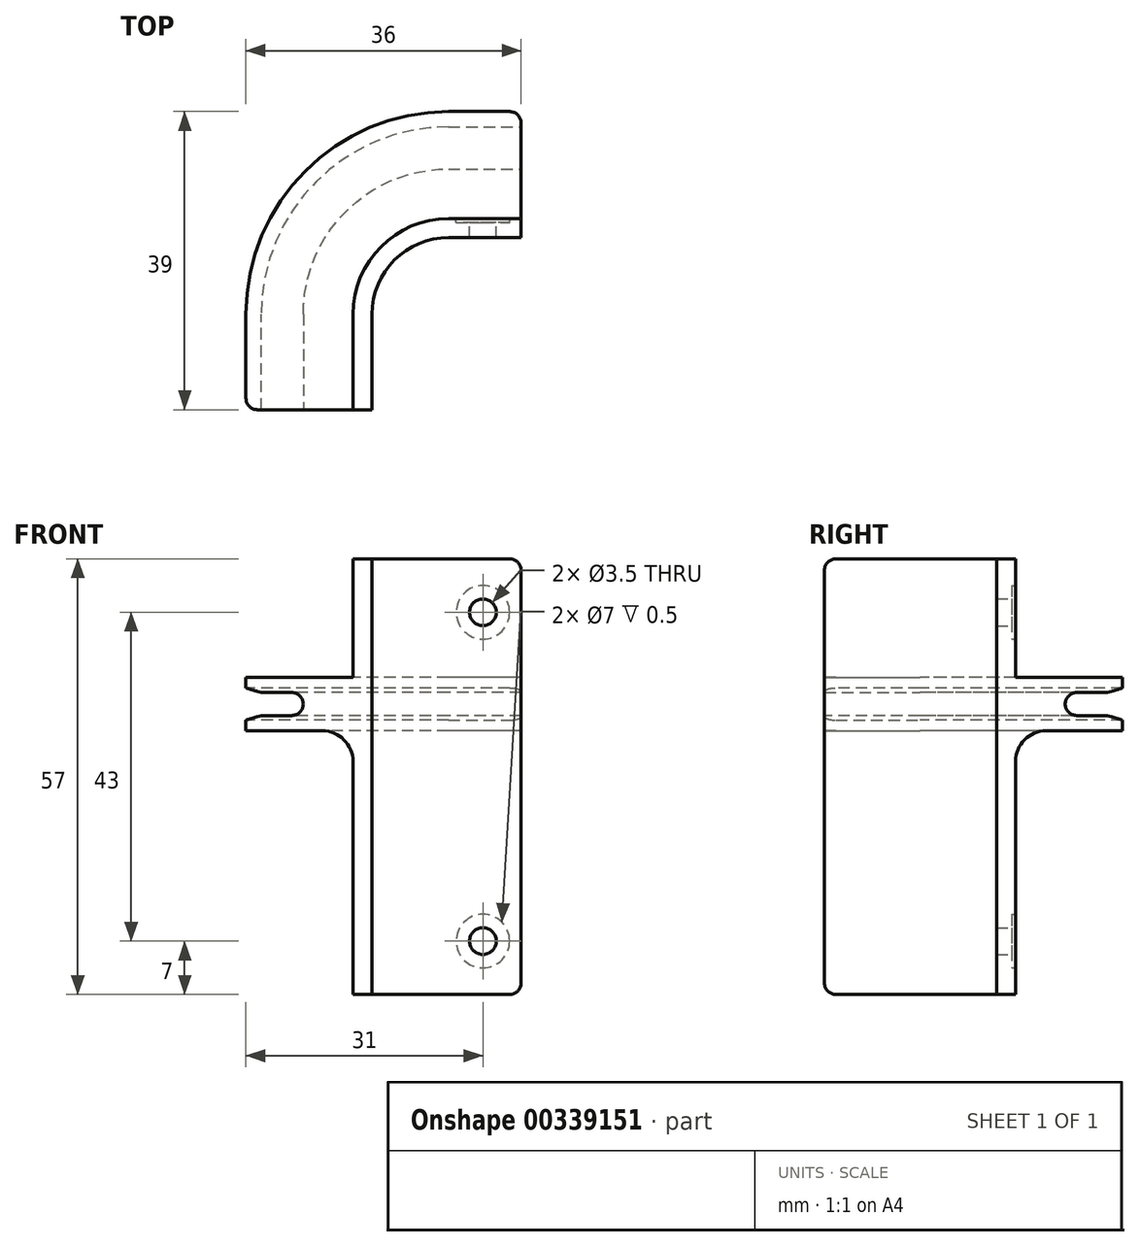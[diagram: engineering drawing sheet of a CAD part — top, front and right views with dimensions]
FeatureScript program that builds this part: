
annotation { "Feature Type Name" : "Feature", "Feature Type Description" : "" }
export const myFeature = defineFeature(function(context is Context, id is Id, definition is map)
    precondition{}
    {
        {
            var Q0;
            Q0=qCreatedBy(makeId("Top.planeOp"),FACE);
            var sketch = newSketch(context, id + "F0", { "sketchPlane" : qUnion([Q0])});
            skArc(sketch, "E0", {"start": v(0, 10) * mm, "mid": v(-7.07, 7.07) * mm, "end": v(-10, 0) * mm});
            skLineSegment(sketch, "E1", {"start": v(0, 10) * mm, "end": v(9.5, 10) * mm});
            skArc(sketch, "E2", {"start": v(0, 12.5) * mm, "mid": v(-8.84, 8.84) * mm, "end": v(-12.5, 0) * mm});
            skLineSegment(sketch, "E3", {"start": v(-12.5, 0) * mm, "end": v(-12.5, -12.5) * mm});
            skLineSegment(sketch, "E4", {"start": v(0, 12.5) * mm, "end": v(9.5, 12.5) * mm});
            skLineSegment(sketch, "E5", {"start": v(-10, 0) * mm, "end": v(-10, -12.5) * mm});
            skLineSegment(sketch, "E6", {"start": v(-10, -12.5) * mm, "end": v(-12.5, -12.5) * mm});
            skLineSegment(sketch, "E7", {"start": v(9.5, 12.5) * mm, "end": v(9.5, 10) * mm});
            skSolve(sketch);
        }
        {
            var Q0;
            Q0=makeQuery(id+"F0.imprint","IMPRINT",FACE,{"disambiguationData":[TD([[makeQuery(id+"F0.imprint","IMPRINT",EDGE,{"derivedFrom":sQuery(id+"F0.wireOp",EDGE,"E0")}),-1.0]])]});
            extrude(context, id + "F1", {"entities" : qUnion([Q0]), "depth" : 40 * mm});
        }
        {
            var Q0;
            Q0=makeQuery(id+"F1.opExtrude","SWEPT_FACE",FACE,{"disambiguationData":[OSD([sQuery(id+"F0.wireOp",EDGE,"E4")])]});
            var sketch = newSketch(context, id + "F2", { "sketchPlane" : qUnion([Q0])});
            skLineSegment(sketch, "E8", {"start": v(-9.5, 24.5) * mm, "end": v(-5.72, 24.5) * mm});
            skLineSegment(sketch, "E9", {"start": v(-9.5, 17.5) * mm, "end": v(-5.74, 17.5) * mm});
            skLineSegment(sketch, "E10", {"start": v(-9.5, 22.5) * mm, "end": v(-5.74, 22.5) * mm});
            skLineSegment(sketch, "E11", {"start": v(-9.5, 19.5) * mm, "end": v(-5.73, 19.5) * mm});
            skPoint(sketch, "E12.orphan", {"position": v(0, 22.5) * mm});
            skPoint(sketch, "E13.orphan", {"position": v(0, 19.5) * mm});
            skPoint(sketch, "E14.orphan", {"position": v(0, 23) * mm});
            skPoint(sketch, "E15.end.orphan", {"position": v(0, 25) * mm});
            skPoint(sketch, "E16.start.orphan", {"position": v(0, 20) * mm});
            skLineSegment(sketch, "E17", {"start": v(-5.72, 24.5) * mm, "end": v(0, 24.5) * mm});
            skLineSegment(sketch, "E18", {"start": v(-5.74, 22.5) * mm, "end": v(0, 22.5) * mm});
            skLineSegment(sketch, "E19", {"start": v(-5.73, 19.5) * mm, "end": v(0, 19.5) * mm});
            skLineSegment(sketch, "E20", {"start": v(-5.74, 17.5) * mm, "end": v(0, 17.5) * mm});
            skSolve(sketch);
        }
        {
            var Q0;
            {var subQ0=sQuery(id+"F2.wireOp",EDGE,"E10");Q0=makeQuery(id+"F2.imprint","IMPRINT",FACE,{"disambiguationData":[TD([[makeQuery(id+"F2.imprint","IMPRINT",EDGE,{"derivedFrom":subQ0}),-1.0]])]});}
            extrude(context, id + "F3", {"entities" : qUnion([Q0]), "operationType" : NewBodyOperationType.ADD, "depth" : 6.5 * mm});
        }
        {
            var Q0;
            {var subQ0=sQuery(id+"F2.wireOp",EDGE,"E8");Q0=makeQuery(id+"F2.imprint","IMPRINT",FACE,{"disambiguationData":[TD([[makeQuery(id+"F2.imprint","IMPRINT",EDGE,{"derivedFrom":subQ0}),-1.0]])]});}
            var Q1;
            {var subQ0=sQuery(id+"F2.wireOp",EDGE,"E9");Q1=makeQuery(id+"F2.imprint","IMPRINT",FACE,{"disambiguationData":[TD([[makeQuery(id+"F2.imprint","IMPRINT",EDGE,{"derivedFrom":subQ0}),1.0]])]});}
            extrude(context, id + "F4", {"entities" : qUnion([Q0, Q1]), "operationType" : NewBodyOperationType.ADD, "depth" : 14 * mm});
        }
        {
            var Q0;
            {var subQ4=sQuery(id+"F2.wireOp",EDGE,"E8");Q0=makeQuery(id+"F2.imprint","IMPRINT",FACE,{"disambiguationData":[TD([[makeQuery(id+"F2.imprint","IMPRINT",EDGE,{"derivedFrom":subQ4}),1.0]])]});}
            var sketch = newSketch(context, id + "F5", { "sketchPlane" : qUnion([Q0])});
            skCircle(sketch, "E21", {"center": v(-4.5, 33) * mm, "radius": 3.5 * mm});
            skCircle(sketch, "E22", {"center": v(-4.5, 33) * mm, "radius": 1.75 * mm});
            skSolve(sketch);
        }
        {
            var Q0;
            Q0=makeQuery(id+"F5.imprint","IMPRINT",FACE,{"disambiguationData":[TD([[makeQuery(id+"F5.imprint","IMPRINT",EDGE,{"derivedFrom":sQuery(id+"F5.wireOp",EDGE,"E21")}),1.0]])]});
            extrude(context, id + "F6", {"entities" : qUnion([Q0]), "operationType" : NewBodyOperationType.REMOVE, "oppositeDirection" : true, "depth" : 0.5 * mm});
        }
        {
            var Q0;
            Q0=makeQuery(id+"F5.imprint","IMPRINT",FACE,{"disambiguationData":[TD([[makeQuery(id+"F5.imprint","IMPRINT",EDGE,{"derivedFrom":sQuery(id+"F5.wireOp",EDGE,"E22")}),1.0]])]});
            extrude(context, id + "F7", {"entities" : qUnion([Q0]), "operationType" : NewBodyOperationType.REMOVE, "oppositeDirection" : true, "depth" : 25 * mm});
        }
        {
            var Q0;
            Q0=makeQuery(id+"F1.opExtrude","CAP_FACE",FACE,{"disambiguationData":[OSD([sQuery(id+"F0.wireOp",EDGE,"E0"),sQuery(id+"F0.wireOp",EDGE,"E1"),sQuery(id+"F0.wireOp",EDGE,"E2"),sQuery(id+"F0.wireOp",EDGE,"E3"),sQuery(id+"F0.wireOp",EDGE,"E4"),sQuery(id+"F0.wireOp",EDGE,"E5"),sQuery(id+"F0.wireOp",EDGE,"E6"),sQuery(id+"F0.wireOp",EDGE,"E7")])],"isStart":true});
            extrude(context, id + "F8", {"entities" : qUnion([Q0]), "operationType" : NewBodyOperationType.ADD, "depth" : 17 * mm});
        }
        {
            var Q0;
            {var subQ0=sQuery(id+"F0.wireOp",EDGE,"E4");Q0=makeQuery(id+"F8.boolean.opBoolean","MERGE",FACE,{"derivedFrom":[makeQuery(id+"F3.boolean.opBoolean","SPLIT",FACE,{"disambiguationData":[TD([makeQuery(id+"F3.opExtrude","SWEPT_FACE",FACE,{"disambiguationData":[OSD([sQuery(id+"F2.wireOp",EDGE,"E11"),sQuery(id+"F2.wireOp",EDGE,"E19")])]})])],"derivedFrom":makeQuery(id+"F1.opExtrude","SWEPT_FACE",FACE,{"disambiguationData":[OSD([subQ0])]})}),makeQuery(id+"F8.opExtrude","SWEPT_FACE",FACE,{"disambiguationData":[OSD([subQ0])]})]});}
            var sketch = newSketch(context, id + "F9", { "sketchPlane" : qUnion([Q0])});
            skCircle(sketch, "E23", {"center": v(-4.5, -10) * mm, "radius": 3.5 * mm});
            skCircle(sketch, "E24", {"center": v(-4.5, -10) * mm, "radius": 1.75 * mm});
            skSolve(sketch);
        }
        {
            var Q0;
            Q0=makeQuery(id+"F9.imprint","IMPRINT",FACE,{"disambiguationData":[TD([[makeQuery(id+"F9.imprint","IMPRINT",EDGE,{"derivedFrom":sQuery(id+"F9.wireOp",EDGE,"E24")}),1.0]])]});
            extrude(context, id + "F10", {"entities" : qUnion([Q0]), "operationType" : NewBodyOperationType.REMOVE, "oppositeDirection" : true, "depth" : 3 * mm});
        }
        {
            var Q0;
            Q0=makeQuery(id+"F9.imprint","IMPRINT",FACE,{"disambiguationData":[TD([[makeQuery(id+"F9.imprint","IMPRINT",EDGE,{"derivedFrom":sQuery(id+"F9.wireOp",EDGE,"E23")}),1.0]])]});
            extrude(context, id + "F11", {"entities" : qUnion([Q0]), "operationType" : NewBodyOperationType.REMOVE, "oppositeDirection" : true, "depth" : 0.5 * mm});
        }
        {
            var Q0;
            {var subQ0=sQuery(id+"F0.wireOp",EDGE,"E3");Q0=makeQuery(id+"F8.boolean.opBoolean","MERGE",FACE,{"derivedFrom":[makeQuery(id+"F1.opExtrude","SWEPT_FACE",FACE,{"disambiguationData":[OSD([subQ0])]}),makeQuery(id+"F8.opExtrude","SWEPT_FACE",FACE,{"disambiguationData":[OSD([subQ0])]})]});}
            var sketch = newSketch(context, id + "F12", { "sketchPlane" : qUnion([Q0])});
            skLineSegment(sketch, "E25", {"start": v(12.5, 24.5) * mm, "end": v(0, 24.5) * mm});
            skLineSegment(sketch, "E26", {"start": v(12.5, 22.5) * mm, "end": v(0, 22.5) * mm});
            skLineSegment(sketch, "E27", {"start": v(12.5, 19.5) * mm, "end": v(0, 19.5) * mm});
            skLineSegment(sketch, "E28", {"start": v(12.5, 17.5) * mm, "end": v(0, 17.5) * mm});
            skSolve(sketch);
        }
        {
            var Q0;
            {var subQ0=sQuery(id+"F12.wireOp",EDGE,"E26");Q0=makeQuery(id+"F12.imprint","IMPRINT",FACE,{"disambiguationData":[TD([[makeQuery(id+"F12.imprint","IMPRINT",EDGE,{"derivedFrom":subQ0}),1.0]])]});}
            extrude(context, id + "F13", {"entities" : qUnion([Q0]), "operationType" : NewBodyOperationType.ADD, "depth" : 6.5 * mm});
        }
        {
            var Q0;
            {var subQ0=sQuery(id+"F12.wireOp",EDGE,"E25");Q0=makeQuery(id+"F12.imprint","IMPRINT",FACE,{"disambiguationData":[TD([[makeQuery(id+"F12.imprint","IMPRINT",EDGE,{"derivedFrom":subQ0}),1.0]])]});}
            var Q1;
            {var subQ0=sQuery(id+"F12.wireOp",EDGE,"E27");Q1=makeQuery(id+"F12.imprint","IMPRINT",FACE,{"disambiguationData":[TD([[makeQuery(id+"F12.imprint","IMPRINT",EDGE,{"derivedFrom":subQ0}),1.0]])]});}
            extrude(context, id + "F14", {"entities" : qUnion([Q0, Q1]), "operationType" : NewBodyOperationType.ADD, "depth" : 14 * mm});
        }
        {
            var Q0;
            {var subQ0=sQuery(id+"F0.wireOp",EDGE,"E3");var subQ1=sQuery(id+"F0.wireOp",EDGE,"E2");var subQ2=makeQuery(id+"F8.boolean.opBoolean","MERGE",EDGE,{"derivedFrom":[makeQuery(id+"F1.opExtrude","SWEPT_EDGE",EDGE,{"disambiguationData":[OSD([subQ1,subQ0])]}),makeQuery(id+"F8.opExtrude","SWEPT_EDGE",EDGE,{"disambiguationData":[OSD([subQ1,subQ0])]})]});Q0=makeQuery(id+"F14.boolean.opBoolean","MERGE",FACE,{"derivedFrom":[makeQuery(id+"F13.opExtrude","SWEPT_FACE",FACE,{"disambiguationData":[OSD([subQ1,subQ0])]}),makeQuery(id+"F14.opExtrude","SWEPT_FACE",FACE,{"disambiguationData":[OSD([subQ1,subQ0]),TDD([makeQuery(id+"F12.imprint","IMPRINT",EDGE,{"disambiguationData":[TD([[makeQuery(id+"F12.imprint","INTERSECT",VERTEX,{"derivedFrom":[subQ2,sQuery(id+"F12.wireOp",EDGE,"E25")]}),-1.0]])],"derivedFrom":subQ2})])]}),makeQuery(id+"F14.opExtrude","SWEPT_FACE",FACE,{"disambiguationData":[OSD([subQ1,subQ0]),TDD([makeQuery(id+"F12.imprint","IMPRINT",EDGE,{"disambiguationData":[TD([[makeQuery(id+"F12.imprint","INTERSECT",VERTEX,{"derivedFrom":[subQ2,sQuery(id+"F12.wireOp",EDGE,"E27")]}),-1.0]])],"derivedFrom":subQ2})])]})]});}
            var Q1;
            {var subQ0=sQuery(id+"F0.wireOp",EDGE,"E2");Q1=makeQuery(id+"F8.boolean.opBoolean","MERGE",FACE,{"derivedFrom":[makeQuery(id+"F1.opExtrude","SWEPT_FACE",FACE,{"disambiguationData":[OSD([subQ0])]}),makeQuery(id+"F8.opExtrude","SWEPT_FACE",FACE,{"disambiguationData":[OSD([subQ0])]})]});}
            revolve(context, id + "F15", {"operationType" : NewBodyOperationType.ADD, "entities" : qUnion([Q0]), "axis" : qUnion([Q1]), "revolveType" : RevolveType.ONE_DIRECTION, "angle" : 90 * degree});
        }
        {
            var Q0;
            {var subQ0=sQuery(id+"F12.wireOp",EDGE,"E28");var subQ1=sQuery(id+"F0.wireOp",EDGE,"E3");var subQ2=sQuery(id+"F0.wireOp",EDGE,"E2");Q0=makeQuery(id+"F15.opRevolve","SWEPT_EDGE",EDGE,{"disambiguationData":[OSD([subQ2,subQ1,subQ0]),TDD([makeQuery(id+"F14.opExtrude","CAP_VERTEX",VERTEX,{"disambiguationData":[OSD([subQ2,subQ1,subQ0])],"isStart":true})])]});}
            var Q1;
            {var subQ0=sQuery(id+"F12.wireOp",EDGE,"E25");var subQ1=sQuery(id+"F0.wireOp",EDGE,"E3");var subQ2=sQuery(id+"F0.wireOp",EDGE,"E2");Q1=makeQuery(id+"F15.opRevolve","SWEPT_EDGE",EDGE,{"disambiguationData":[OSD([subQ2,subQ1,subQ0]),TDD([makeQuery(id+"F14.opExtrude","CAP_VERTEX",VERTEX,{"disambiguationData":[OSD([subQ2,subQ1,subQ0])],"isStart":true})])]});}
            fillet(context, id + "F16", {"entities" : qUnion([Q0, Q1]), "radius" : 4 * mm, "tangentPropagation" : true, "allowEdgeOverflow" : false});
        }
        {
            var Q0;
            Q0=makeQuery(id+"F14.opExtrude","CAP_EDGE",EDGE,{"disambiguationData":[OSD([sQuery(id+"F12.wireOp",EDGE,"E27")])],"isStart":false});
            chamfer(context, id + "F17", {"entities" : qUnion([Q0]), "chamferType" : ChamferType.TWO_OFFSETS, "width1" : 0.6 * mm, "oppositeDirection" : false, "width2" : 2 * mm, "tangentPropagation" : true});
        }
        {
            var Q0;
            Q0=makeQuery(id+"F14.opExtrude","CAP_EDGE",EDGE,{"disambiguationData":[OSD([sQuery(id+"F12.wireOp",EDGE,"E26")])],"isStart":false});
            chamfer(context, id + "F18", {"entities" : qUnion([Q0]), "chamferType" : ChamferType.TWO_OFFSETS, "width1" : 2 * mm, "oppositeDirection" : false, "width2" : 0.6 * mm, "tangentPropagation" : true});
        }
        {
            var Q0;
            {var subQ0=sQuery(id+"F12.wireOp",EDGE,"E27");var subQ1=sQuery(id+"F0.wireOp",EDGE,"E3");var subQ2=sQuery(id+"F0.wireOp",EDGE,"E2");Q0=makeQuery(id+"F15.opRevolve","SWEPT_EDGE",EDGE,{"disambiguationData":[OSD([subQ2,subQ1,subQ0]),TDD([makeQuery(id+"F13.opExtrude","CAP_VERTEX",VERTEX,{"disambiguationData":[OSD([subQ2,subQ1,subQ0])],"isStart":false})])]});}
            var Q1;
            {var subQ0=sQuery(id+"F12.wireOp",EDGE,"E26");var subQ1=sQuery(id+"F0.wireOp",EDGE,"E3");var subQ2=sQuery(id+"F0.wireOp",EDGE,"E2");Q1=makeQuery(id+"F15.opRevolve","SWEPT_EDGE",EDGE,{"disambiguationData":[OSD([subQ2,subQ1,subQ0]),TDD([makeQuery(id+"F13.opExtrude","CAP_VERTEX",VERTEX,{"disambiguationData":[OSD([subQ2,subQ1,subQ0])],"isStart":false})])]});}
            var Q2;
            {var subQ0=sQuery(id+"F0.wireOp",EDGE,"E7");var subQ1=sQuery(id+"F0.wireOp",EDGE,"E4");var subQ2=makeQuery(id+"F1.opExtrude","SWEPT_EDGE",EDGE,{"disambiguationData":[OSD([subQ1,subQ0])]});Q2=makeQuery(id+"F4.opExtrude","CAP_EDGE",EDGE,{"disambiguationData":[OSD([subQ1,subQ0]),TDD([makeQuery(id+"F2.imprint","IMPRINT",EDGE,{"disambiguationData":[TD([[makeQuery(id+"F2.imprint","INTERSECT",VERTEX,{"derivedFrom":[subQ2,sQuery(id+"F2.wireOp",EDGE,"E8")]}),-1.0]])],"derivedFrom":subQ2})])],"isStart":false});}
            var Q3;
            {var subQ0=sQuery(id+"F0.wireOp",EDGE,"E7");var subQ1=sQuery(id+"F0.wireOp",EDGE,"E4");var subQ2=makeQuery(id+"F1.opExtrude","SWEPT_EDGE",EDGE,{"disambiguationData":[OSD([subQ1,subQ0])]});Q3=makeQuery(id+"F4.opExtrude","CAP_EDGE",EDGE,{"disambiguationData":[OSD([subQ1,subQ0]),TDD([makeQuery(id+"F2.imprint","IMPRINT",EDGE,{"disambiguationData":[TD([[makeQuery(id+"F2.imprint","INTERSECT",VERTEX,{"derivedFrom":[subQ2,sQuery(id+"F2.wireOp",EDGE,"E9")]}),1.0]])],"derivedFrom":subQ2})])],"isStart":false});}
            var Q4;
            {var subQ0=sQuery(id+"F0.wireOp",EDGE,"E6");var subQ1=sQuery(id+"F0.wireOp",EDGE,"E3");var subQ2=makeQuery(id+"F8.boolean.opBoolean","MERGE",EDGE,{"derivedFrom":[makeQuery(id+"F1.opExtrude","SWEPT_EDGE",EDGE,{"disambiguationData":[OSD([subQ1,subQ0])]}),makeQuery(id+"F8.opExtrude","SWEPT_EDGE",EDGE,{"disambiguationData":[OSD([subQ1,subQ0])]})]});Q4=makeQuery(id+"F14.opExtrude","CAP_EDGE",EDGE,{"disambiguationData":[OSD([subQ1,subQ0]),TDD([makeQuery(id+"F12.imprint","IMPRINT",EDGE,{"disambiguationData":[TD([[makeQuery(id+"F12.imprint","INTERSECT",VERTEX,{"derivedFrom":[subQ2,sQuery(id+"F12.wireOp",EDGE,"E27")]}),-1.0]])],"derivedFrom":subQ2})])],"isStart":false});}
            var Q5;
            {var subQ0=sQuery(id+"F0.wireOp",EDGE,"E6");var subQ1=sQuery(id+"F0.wireOp",EDGE,"E3");var subQ2=makeQuery(id+"F8.boolean.opBoolean","MERGE",EDGE,{"derivedFrom":[makeQuery(id+"F1.opExtrude","SWEPT_EDGE",EDGE,{"disambiguationData":[OSD([subQ1,subQ0])]}),makeQuery(id+"F8.opExtrude","SWEPT_EDGE",EDGE,{"disambiguationData":[OSD([subQ1,subQ0])]})]});Q5=makeQuery(id+"F14.opExtrude","CAP_EDGE",EDGE,{"disambiguationData":[OSD([subQ1,subQ0]),TDD([makeQuery(id+"F12.imprint","IMPRINT",EDGE,{"disambiguationData":[TD([[makeQuery(id+"F12.imprint","INTERSECT",VERTEX,{"derivedFrom":[subQ2,sQuery(id+"F12.wireOp",EDGE,"E25")]}),-1.0]])],"derivedFrom":subQ2})])],"isStart":false});}
            var Q6;
            Q6=makeQuery(id+"F1.opExtrude","CAP_EDGE",EDGE,{"disambiguationData":[OSD([sQuery(id+"F0.wireOp",EDGE,"E6")])],"isStart":false});
            var Q7;
            Q7=makeQuery(id+"F1.opExtrude","CAP_EDGE",EDGE,{"disambiguationData":[OSD([sQuery(id+"F0.wireOp",EDGE,"E7")])],"isStart":false});
            var Q8;
            Q8=makeQuery(id+"F8.opExtrude","CAP_EDGE",EDGE,{"disambiguationData":[OSD([sQuery(id+"F0.wireOp",EDGE,"E7")])],"isStart":false});
            var Q9;
            Q9=makeQuery(id+"F8.opExtrude","CAP_EDGE",EDGE,{"disambiguationData":[OSD([sQuery(id+"F0.wireOp",EDGE,"E6")])],"isStart":false});
            fillet(context, id + "F19", {"entities" : qUnion([Q0, Q1, Q2, Q3, Q4, Q5, Q6, Q7, Q8, Q9]), "radius" : 1.5 * mm, "tangentPropagation" : true, "allowEdgeOverflow" : false});
        }
    });
